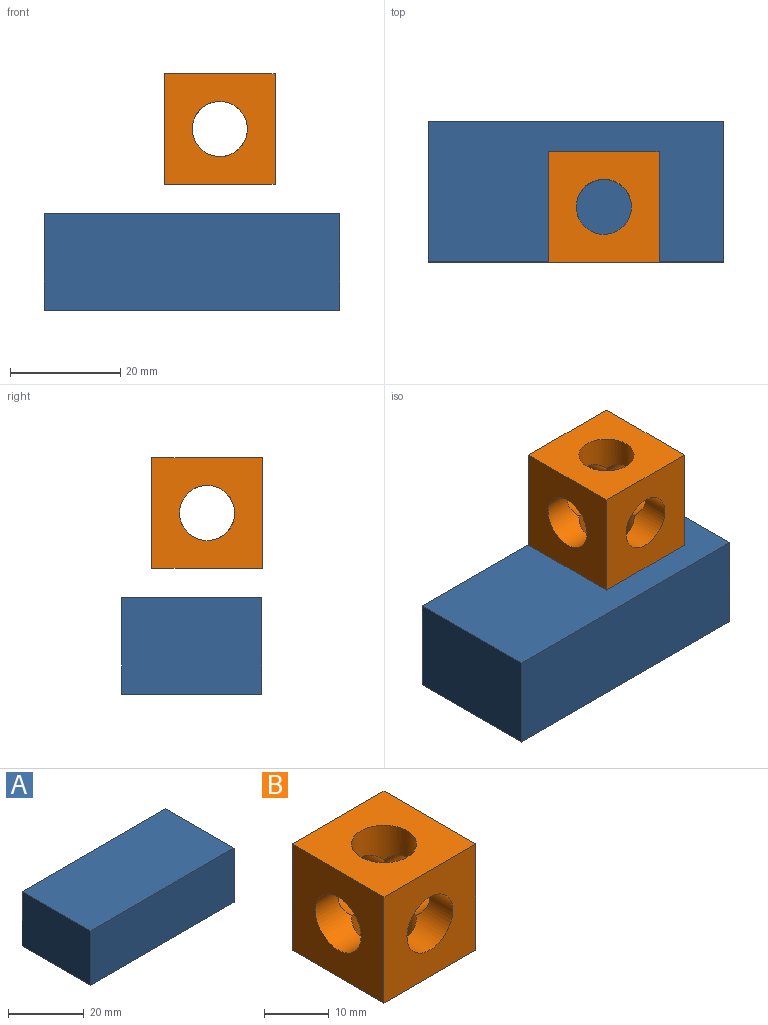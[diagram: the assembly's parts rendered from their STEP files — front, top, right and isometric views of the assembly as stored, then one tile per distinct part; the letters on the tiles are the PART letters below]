
ASSEMBLY  parts=2 mates=1
PART A: 6 faces, bbox 53.5x25.4x17.5 mm
  f0: plane 25.4x17.51mm, normal (-1,0,0), area 444.9mm2, adj f1,f3,f4,f5
  f1: plane 53.54x25.4mm, normal (0,0,-1), area 1359.9mm2, adj f0,f2,f4,f5
  f2: plane 25.4x17.51mm, normal (1,0,0), area 444.9mm2, adj f1,f3,f4,f5
  f3: plane 53.54x25.4mm, normal (0,0,1), area 1359.9mm2, adj f0,f2,f4,f5
  f4: plane 53.54x17.51mm, normal (0,-1,0), area 937.7mm2, adj f0,f1,f2,f3
  f5: plane 53.54x17.51mm, normal (0,1,0), area 937.7mm2, adj f0,f1,f2,f3
PART B: 12 faces, bbox 20x20x20 mm
  f0: cylinder r=5mm len=10mm, axis (0,1,0), area 172.7mm2, adj f6,f8,f9,f10,f11
  f1: plane 20x20mm, normal (0,0,1), area 321.5mm2, adj f2,f5,f6,f7,f10
  f2: plane 20x20mm, normal (-1,0,0), area 321.5mm2, adj f1,f3,f6,f7,f9
  f3: plane 20x20mm, normal (0,0,-1), area 321.5mm2, adj f2,f5,f6,f7,f11
  f4: cylinder r=5mm len=10mm, axis (0,1,0), area 172.7mm2, adj f7,f8,f9,f10,f11
  f5: plane 20x20mm, normal (1,0,0), area 321.5mm2, adj f1,f3,f6,f7,f8
  f6: plane 20x20mm, normal (0,-1,0), area 321.5mm2, adj f0,f1,f2,f3,f5
  f7: plane 20x20mm, normal (0,1,0), area 321.5mm2, adj f1,f2,f3,f4,f5
  f8: cylinder r=5mm len=10mm, axis (-1,0,0), area 172.7mm2, adj f0,f4,f5,f10,f11
  f9: cylinder r=5mm len=10mm, axis (-1,0,0), area 172.7mm2, adj f0,f2,f4,f10,f11
  f10: cylinder r=5mm len=10mm, axis (0,0,1), area 172.7mm2, adj f0,f1,f4,f8,f9
  f11: cylinder r=5mm len=10mm, axis (0,0,1), area 172.7mm2, adj f0,f3,f4,f8,f9
PLACE A t=(35.05,1.53,-53.49)mm
PLACE B rot(axis=(1,0,0),180deg) t=(-13.17,-23.95,35.22)mm
MATE parallel B.f10 <-> A.f3  axis (0,0,-1) through (-8.55,-13.95,9.11)mm
